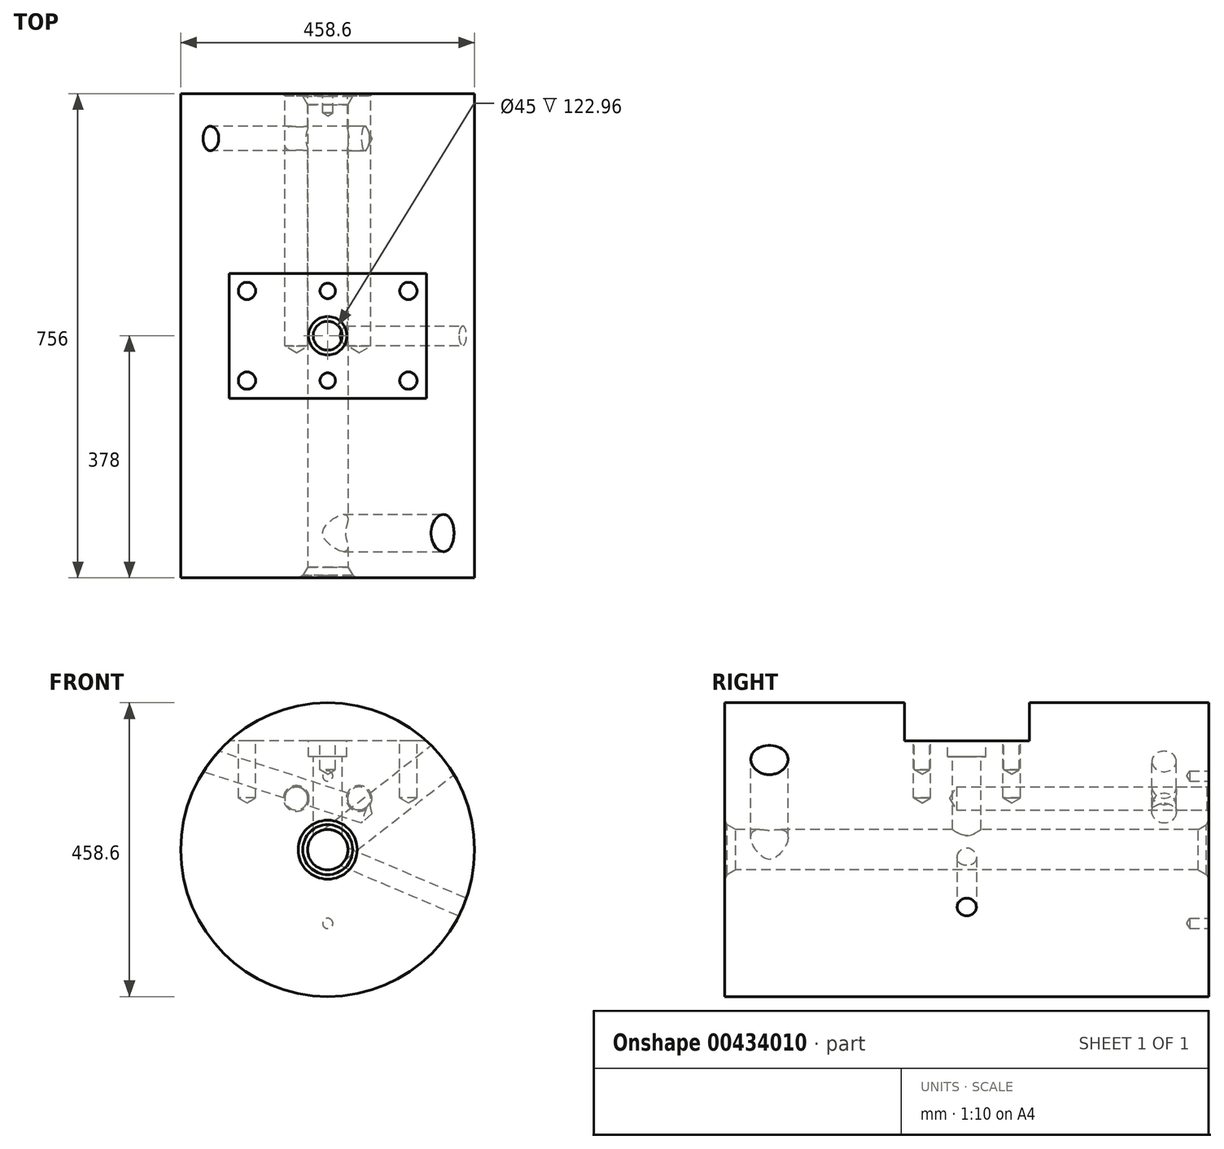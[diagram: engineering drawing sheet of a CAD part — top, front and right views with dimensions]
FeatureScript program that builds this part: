
annotation { "Feature Type Name" : "Feature", "Feature Type Description" : "" }
export const myFeature = defineFeature(function(context is Context, id is Id, definition is map)
    precondition{}
    {
        {
            var Q0;
            Q0=qCreatedBy(makeId("Front.planeOp"),FACE);
            var sketch = newSketch(context, id + "F0", { "sketchPlane" : qUnion([Q0])});
            skCircle(sketch, "E0", {"center": v(0, 0) * mm, "radius": 229.3 * mm});
            skSolve(sketch);
        }
        {
            var Q0;
            Q0=qCreatedBy(makeId("Right.planeOp"),FACE);
            var sketch = newSketch(context, id + "F1", { "sketchPlane" : qUnion([Q0])});
            skLineSegment(sketch, "E1", {"start": v(0, 0) * mm, "end": v(756, 0) * mm});
            skLineSegment(sketch, "E2", {"start": v(0, 0) * mm, "end": v(0, 229.3) * mm});
            skLineSegment(sketch, "E3", {"start": v(0, 229.3) * mm, "end": v(756, 229.3) * mm});
            skLineSegment(sketch, "E4", {"start": v(756, 0) * mm, "end": v(756, 229.3) * mm});
            skLineSegment(sketch, "E5.0", {"start": v(0, 31.5) * mm, "end": v(756, 31.5) * mm});
            skLineSegment(sketch, "E6", {"start": v(0, 46) * mm, "end": v(4, 39) * mm});
            skLineSegment(sketch, "E7", {"start": v(4, 39) * mm, "end": v(17, 31.5) * mm});
            skLineSegment(sketch, "E8", {"start": v(378, 229.3) * mm, "end": v(378, 142.86) * mm});
            skLineSegment(sketch, "E9.MirrorCS", {"start": v(756, 46) * mm, "end": v(752, 39) * mm});
            skLineSegment(sketch, "E10.MirrorCS", {"start": v(752, 39) * mm, "end": v(739, 31.5) * mm});
            skSolve(sketch);
        }
        {
            var Q0;
            {var subQ8=sQuery(id+"F1.wireOp",EDGE,"E6");Q0=makeQuery(id+"F1.imprint","IMPRINT",FACE,{"disambiguationData":[TD([[makeQuery(id+"F1.imprint","IMPRINT",EDGE,{"derivedFrom":subQ8}),1.0]])]});}
            var Q1;
            Q1=sQuery(id+"F1.wireOp",EDGE,"E1");
            revolve(context, id + "F2", {"entities" : qUnion([Q0]), "axis" : qUnion([Q1]), "revolveType" : RevolveType.FULL});
        }
        {
            var Q0;
            Q0=qCreatedBy(makeId("Right.planeOp"),FACE);
            var sketch = newSketch(context, id + "F3", { "sketchPlane" : qUnion([Q0])});
            skLineSegment(sketch, "E11", {"start": v(0, -229.3) * mm, "end": v(756, -229.3) * mm});
            skLineSegment(sketch, "E12", {"start": v(756, 229.3) * mm, "end": v(0, 229.3) * mm});
            skLineSegment(sketch, "E13", {"start": v(0, 0) * mm, "end": v(676.75, 0) * mm});
            skLineSegment(sketch, "E14.0", {"start": v(0, 170) * mm, "end": v(676.75, 170) * mm});
            skLineSegment(sketch, "E15", {"start": v(378, 229.3) * mm, "end": v(378, 170) * mm});
            skLineSegment(sketch, "E16.0", {"start": v(280.5, 229.3) * mm, "end": v(280.5, 170) * mm});
            skLineSegment(sketch, "E17.0", {"start": v(475.5, 229.3) * mm, "end": v(475.5, 170) * mm});
            skSolve(sketch);
        }
        {
            var Q0;
            {var subQ0=sQuery(id+"F3.wireOp",EDGE,"E15");Q0=makeQuery(id+"F3.imprint","IMPRINT",FACE,{"disambiguationData":[TD([[makeQuery(id+"F3.imprint","IMPRINT",EDGE,{"derivedFrom":subQ0}),-1.0]])]});}
            var Q1;
            {var subQ0=sQuery(id+"F3.wireOp",EDGE,"E15");Q1=makeQuery(id+"F3.imprint","IMPRINT",FACE,{"disambiguationData":[TD([[makeQuery(id+"F3.imprint","IMPRINT",EDGE,{"derivedFrom":subQ0}),1.0]])]});}
            extrude(context, id + "F4", {"entities" : qUnion([Q0, Q1]), "operationType" : NewBodyOperationType.REMOVE, "endBound" : BoundingType.SYMMETRIC, "depth" : 400 * mm});
        }
        {
            var Q0;
            Q0=makeQuery(id+"F4.boolean.opBoolean","COPY",FACE,{"derivedFrom":makeQuery(id+"F4.opExtrude","SWEPT_FACE",FACE,{"disambiguationData":[OSD([sQuery(id+"F3.wireOp",EDGE,"E14.0")])]})});
            var sketch = newSketch(context, id + "F5", { "sketchPlane" : qUnion([Q0])});
            skLineSegment(sketch, "E18", {"start": v(153.88, 0) * mm, "end": v(153.88, 280.5) * mm});
            skLineSegment(sketch, "E19", {"start": v(153.88, 280.5) * mm, "end": v(153.88, 475.5) * mm});
            skLineSegment(sketch, "E20", {"start": v(153.88, 475.5) * mm, "end": v(153.88, 756) * mm});
            skLineSegment(sketch, "E21", {"start": v(-153.88, 280.5) * mm, "end": v(-153.88, 0) * mm});
            skLineSegment(sketch, "E22", {"start": v(-153.88, 475.5) * mm, "end": v(-153.88, 280.5) * mm});
            skLineSegment(sketch, "E23", {"start": v(-153.88, 756) * mm, "end": v(-153.88, 475.5) * mm});
            skLineSegment(sketch, "E24", {"start": v(153.88, 280.5) * mm, "end": v(-153.88, 280.5) * mm});
            skLineSegment(sketch, "E25", {"start": v(153.88, 475.5) * mm, "end": v(153.88, 280.5) * mm});
            skLineSegment(sketch, "E26", {"start": v(153.88, 475.5) * mm, "end": v(-153.88, 475.5) * mm});
            skLineSegment(sketch, "E27", {"start": v(-153.88, 280.5) * mm, "end": v(-153.88, 475.5) * mm});
            skPoint(sketch, "E28", {"position": v(-126, 308) * mm});
            skPoint(sketch, "E29", {"position": v(0, 308) * mm});
            skPoint(sketch, "E30", {"position": v(126, 308) * mm});
            skPoint(sketch, "E31", {"position": v(-66, 378) * mm});
            skPoint(sketch, "E32", {"position": v(0, 378) * mm});
            skPoint(sketch, "E33", {"position": v(66, 378) * mm});
            skPoint(sketch, "E34", {"position": v(-153.88, 378) * mm});
            skLineSegment(sketch, "E35", {"start": v(-153.88, 378) * mm, "end": v(153.88, 378) * mm, "construction": true});
            skPoint(sketch, "E36", {"position": v(0, 280.5) * mm});
            skLineSegment(sketch, "E37", {"start": v(0, 280.5) * mm, "end": v(0, 378) * mm, "construction": true});
            skPoint(sketch, "E38.MirrorP", {"position": v(-126, 448) * mm});
            skPoint(sketch, "E39.MirrorP", {"position": v(0, 448) * mm});
            skPoint(sketch, "E40.MirrorP", {"position": v(126, 448) * mm});
            skSolve(sketch);
        }
        {
            var Q0;
            Q0=sQuery(id+"F5.wireOp",VERTEX,"E32");
            var Q1;
            Q1=makeQuery(id+"F2.opRevolve","SWEPT_BODY",BODY,{"disambiguationData":[OSD([sQuery(id+"F1.wireOp",EDGE,"E2"),sQuery(id+"F1.wireOp",EDGE,"E3"),sQuery(id+"F1.wireOp",EDGE,"E4"),sQuery(id+"F1.wireOp",EDGE,"E5.0"),sQuery(id+"F1.wireOp",EDGE,"E6"),sQuery(id+"F1.wireOp",EDGE,"E7"),sQuery(id+"F1.wireOp",EDGE,"E9.MirrorCS"),sQuery(id+"F1.wireOp",EDGE,"E10.MirrorCS")])]});
            hole(context, id + "F6", {"style" : HoleStyle.C_BORE, "endStyle" : HoleEndStyle.BLIND, "holeDiameter" : 45 * mm, "cBoreDiameter" : 60 * mm, "cBoreDepth" : 25 * mm, "holeDepth" : 170 * mm, "tappedDepth" : 12 * mm, "tapClearance" : 3, "startFromSketch" : true, "locations" : qUnion([Q0]), "scope" : qUnion([Q1])});
        }
        {
            var Q0;
            Q0=sQuery(id+"F5.wireOp",VERTEX,"E29");
            var Q1;
            Q1=sQuery(id+"F5.wireOp",VERTEX,"E39.MirrorP");
            var Q2;
            Q2=makeQuery(id+"F2.opRevolve","SWEPT_BODY",BODY,{"disambiguationData":[OSD([sQuery(id+"F1.wireOp",EDGE,"E2"),sQuery(id+"F1.wireOp",EDGE,"E3"),sQuery(id+"F1.wireOp",EDGE,"E4"),sQuery(id+"F1.wireOp",EDGE,"E5.0"),sQuery(id+"F1.wireOp",EDGE,"E6"),sQuery(id+"F1.wireOp",EDGE,"E7"),sQuery(id+"F1.wireOp",EDGE,"E9.MirrorCS"),sQuery(id+"F1.wireOp",EDGE,"E10.MirrorCS")])]});
            hole(context, id + "F7", {"style" : HoleStyle.SIMPLE, "endStyle" : HoleEndStyle.BLIND, "holeDiameter" : 24 * mm, "holeDepth" : 45 * mm, "tappedDepth" : 12 * mm, "tapClearance" : 3, "startFromSketch" : true, "locations" : qUnion([Q0, Q1]), "scope" : qUnion([Q2])});
        }
        {
            var Q0;
            Q0=sQuery(id+"F5.wireOp",VERTEX,"E28");
            var Q1;
            Q1=sQuery(id+"F5.wireOp",VERTEX,"E38.MirrorP");
            var Q2;
            Q2=sQuery(id+"F5.wireOp",VERTEX,"E40.MirrorP");
            var Q3;
            Q3=sQuery(id+"F5.wireOp",VERTEX,"E30");
            var Q4;
            Q4=makeQuery(id+"F2.opRevolve","SWEPT_BODY",BODY,{"disambiguationData":[OSD([sQuery(id+"F1.wireOp",EDGE,"E2"),sQuery(id+"F1.wireOp",EDGE,"E3"),sQuery(id+"F1.wireOp",EDGE,"E4"),sQuery(id+"F1.wireOp",EDGE,"E5.0"),sQuery(id+"F1.wireOp",EDGE,"E6"),sQuery(id+"F1.wireOp",EDGE,"E7"),sQuery(id+"F1.wireOp",EDGE,"E9.MirrorCS"),sQuery(id+"F1.wireOp",EDGE,"E10.MirrorCS")])]});
            hole(context, id + "F8", {"style" : HoleStyle.SIMPLE, "endStyle" : HoleEndStyle.BLIND, "holeDiameter" : 27 * mm, "holeDepth" : 89 * mm, "tappedDepth" : 12 * mm, "tapClearance" : 3, "startFromSketch" : true, "locations" : qUnion([Q0, Q1, Q2, Q3]), "scope" : qUnion([Q4])});
        }
        {
            var Q0;
            Q0=sQuery(id+"F5.wireOp",EDGE,"E35");
            cPlane(context, id + "F9", {"entities" : qUnion([Q0]), "cplaneType" : CPlaneType.LINE_ANGLE, "offset" : 25 * mm, "angle" : 0 * degree, "width" : 150 * mm, "height" : 150 * mm});
        }
        {
            var Q0;
            Q0=qCreatedBy(id+"F9.planeOp",FACE);
            var sketch = newSketch(context, id + "F10", { "sketchPlane" : qUnion([Q0])});
            skArc(sketch, "E41", {"start": v(-153.88, 170) * mm, "mid": v(0, -229.3) * mm, "end": v(153.88, 170) * mm});
            skLineSegment(sketch, "E42", {"start": v(153.88, 170) * mm, "end": v(-153.88, 170) * mm});
            skLineSegment(sketch, "E43", {"start": v(0, 0) * mm, "end": v(-211.07, -89.6) * mm});
            skPoint(sketch, "E44", {"position": v(-211.07, -89.6) * mm});
            skSolve(sketch);
        }
        {
            var Q0;
            Q0=sQuery(id+"F10.wireOp",VERTEX,"E44");
            var Q1;
            Q1=sQuery(id+"F10.wireOp",EDGE,"E43");
            cPlane(context, id + "F11", {"entities" : qUnion([Q0, Q1]), "cplaneType" : CPlaneType.LINE_POINT, "offset" : 25 * mm, "width" : 150 * mm, "height" : 150 * mm});
        }
        {
            var Q0;
            Q0=qCreatedBy(id+"F11.planeOp",FACE);
            var sketch = newSketch(context, id + "F12", { "sketchPlane" : qUnion([Q0])});
            skPoint(sketch, "E45.0", {"position": v(378, 0) * mm});
            skSolve(sketch);
        }
        {
            var Q0;
            Q0=sQuery(id+"F12.wireOp",VERTEX,"E45.0");
            var Q1;
            Q1=makeQuery(id+"F2.opRevolve","SWEPT_BODY",BODY,{"disambiguationData":[OSD([sQuery(id+"F1.wireOp",EDGE,"E2"),sQuery(id+"F1.wireOp",EDGE,"E3"),sQuery(id+"F1.wireOp",EDGE,"E4"),sQuery(id+"F1.wireOp",EDGE,"E5.0"),sQuery(id+"F1.wireOp",EDGE,"E6"),sQuery(id+"F1.wireOp",EDGE,"E7"),sQuery(id+"F1.wireOp",EDGE,"E9.MirrorCS"),sQuery(id+"F1.wireOp",EDGE,"E10.MirrorCS")])]});
            hole(context, id + "F13", {"style" : HoleStyle.SIMPLE, "endStyle" : HoleEndStyle.BLIND, "holeDiameter" : 30 * mm, "holeDepth" : 229 * mm, "tappedDepth" : 12 * mm, "tapClearance" : 3, "startFromSketch" : true, "locations" : qUnion([Q0]), "scope" : qUnion([Q1])});
        }
        {
            var Q0;
            Q0=makeQuery(id+"F2.opRevolve","SWEPT_FACE",FACE,{"disambiguationData":[OSD([sQuery(id+"F1.wireOp",EDGE,"E2")])]});
            cPlane(context, id + "F14", {"entities" : qUnion([Q0]), "cplaneType" : CPlaneType.OFFSET, "offset" : 70 * mm, "oppositeDirection" : true, "width" : 150 * mm, "height" : 150 * mm});
        }
        {
            var Q0;
            Q0=qCreatedBy(id+"F14.planeOp",FACE);
            var sketch = newSketch(context, id + "F15", { "sketchPlane" : qUnion([Q0])});
            skCircle(sketch, "E46", {"center": v(0, 0) * mm, "radius": 229.3 * mm});
            skLineSegment(sketch, "E47.0", {"start": v(-153.88, 170) * mm, "end": v(153.88, 170) * mm});
            skLineSegment(sketch, "E48", {"start": v(0, 0) * mm, "end": v(180.7, 141.17) * mm});
            skSolve(sketch);
        }
        {
            var Q0;
            Q0=sQuery(id+"F15.wireOp",VERTEX,"E48.end");
            var Q1;
            Q1=sQuery(id+"F15.wireOp",EDGE,"E48");
            cPlane(context, id + "F16", {"entities" : qUnion([Q0, Q1]), "cplaneType" : CPlaneType.LINE_POINT, "offset" : 25 * mm, "width" : 150 * mm, "height" : 150 * mm});
        }
        {
            var Q0;
            Q0=qCreatedBy(id+"F16.planeOp",FACE);
            var sketch = newSketch(context, id + "F17", { "sketchPlane" : qUnion([Q0])});
            skPoint(sketch, "E49.0", {"position": v(70, 0) * mm});
            skSolve(sketch);
        }
        {
            var Q0;
            Q0=sQuery(id+"F17.wireOp",VERTEX,"E49.0");
            var Q1;
            Q1=makeQuery(id+"F2.opRevolve","SWEPT_BODY",BODY,{"disambiguationData":[OSD([sQuery(id+"F1.wireOp",EDGE,"E2"),sQuery(id+"F1.wireOp",EDGE,"E3"),sQuery(id+"F1.wireOp",EDGE,"E4"),sQuery(id+"F1.wireOp",EDGE,"E5.0"),sQuery(id+"F1.wireOp",EDGE,"E6"),sQuery(id+"F1.wireOp",EDGE,"E7"),sQuery(id+"F1.wireOp",EDGE,"E9.MirrorCS"),sQuery(id+"F1.wireOp",EDGE,"E10.MirrorCS")])]});
            hole(context, id + "F18", {"style" : HoleStyle.SIMPLE, "endStyle" : HoleEndStyle.BLIND, "holeDiameter" : 58 * mm, "holeDepth" : 229 * mm, "tappedDepth" : 12 * mm, "tapClearance" : 3, "startFromSketch" : true, "locations" : qUnion([Q0]), "scope" : qUnion([Q1])});
        }
        {
            var Q0;
            Q0=makeQuery(id+"F2.opRevolve","SWEPT_FACE",FACE,{"disambiguationData":[OSD([sQuery(id+"F1.wireOp",EDGE,"E4")])]});
            cPlane(context, id + "F19", {"entities" : qUnion([Q0]), "cplaneType" : CPlaneType.OFFSET, "offset" : 70 * mm, "oppositeDirection" : true, "width" : 150 * mm, "height" : 150 * mm});
        }
        {
            var Q0;
            Q0=qCreatedBy(id+"F19.planeOp",FACE);
            var sketch = newSketch(context, id + "F20", { "sketchPlane" : qUnion([Q0])});
            skCircle(sketch, "E50", {"center": v(0, 0) * mm, "radius": 229.3 * mm});
            skPoint(sketch, "E51", {"position": v(183.12, 138) * mm});
            skLineSegment(sketch, "E52", {"start": v(183.12, 138) * mm, "end": v(46.4, 93.58) * mm});
            skSolve(sketch);
        }
        {
            var Q0;
            Q0=sQuery(id+"F20.wireOp",VERTEX,"E51");
            var Q1;
            Q1=sQuery(id+"F20.wireOp",EDGE,"E52");
            cPlane(context, id + "F21", {"entities" : qUnion([Q0, Q1]), "cplaneType" : CPlaneType.LINE_POINT, "offset" : 25 * mm, "width" : 150 * mm, "height" : 150 * mm});
        }
        {
            var Q0;
            Q0=qCreatedBy(id+"F21.planeOp",FACE);
            var sketch = newSketch(context, id + "F22", { "sketchPlane" : qUnion([Q0])});
            skPoint(sketch, "E53.0", {"position": v(686, 74.66) * mm});
            skSolve(sketch);
        }
        {
            var Q0;
            Q0=sQuery(id+"F22.wireOp",VERTEX,"E53.0");
            var Q1;
            Q1=makeQuery(id+"F2.opRevolve","SWEPT_BODY",BODY,{"disambiguationData":[OSD([sQuery(id+"F1.wireOp",EDGE,"E2"),sQuery(id+"F1.wireOp",EDGE,"E3"),sQuery(id+"F1.wireOp",EDGE,"E4"),sQuery(id+"F1.wireOp",EDGE,"E5.0"),sQuery(id+"F1.wireOp",EDGE,"E6"),sQuery(id+"F1.wireOp",EDGE,"E7"),sQuery(id+"F1.wireOp",EDGE,"E9.MirrorCS"),sQuery(id+"F1.wireOp",EDGE,"E10.MirrorCS")])]});
            hole(context, id + "F23", {"style" : HoleStyle.SIMPLE, "endStyle" : HoleEndStyle.BLIND, "oppositeDirection" : true, "holeDiameter" : 38 * mm, "holeDepth" : 254 * mm, "tappedDepth" : 12 * mm, "tapClearance" : 3, "startFromSketch" : true, "locations" : qUnion([Q0]), "scope" : qUnion([Q1])});
        }
        {
            var Q0;
            Q0=sQuery(id+"F22.wireOp",VERTEX,"E53.0");
            var Q1;
            Q1=makeQuery(id+"F2.opRevolve","SWEPT_BODY",BODY,{"disambiguationData":[OSD([sQuery(id+"F1.wireOp",EDGE,"E2"),sQuery(id+"F1.wireOp",EDGE,"E3"),sQuery(id+"F1.wireOp",EDGE,"E4"),sQuery(id+"F1.wireOp",EDGE,"E5.0"),sQuery(id+"F1.wireOp",EDGE,"E6"),sQuery(id+"F1.wireOp",EDGE,"E7"),sQuery(id+"F1.wireOp",EDGE,"E9.MirrorCS"),sQuery(id+"F1.wireOp",EDGE,"E10.MirrorCS")])]});
            hole(context, id + "F24", {"style" : HoleStyle.SIMPLE, "endStyle" : HoleEndStyle.BLIND, "holeDiameter" : 38 * mm, "holeDepth" : 50 * mm, "tappedDepth" : 12 * mm, "tapClearance" : 3, "startFromSketch" : true, "locations" : qUnion([Q0]), "scope" : qUnion([Q1])});
        }
        {
            var Q0;
            Q0=makeQuery(id+"F2.opRevolve","SWEPT_FACE",FACE,{"disambiguationData":[OSD([sQuery(id+"F1.wireOp",EDGE,"E4")])]});
            var sketch = newSketch(context, id + "F25", { "sketchPlane" : qUnion([Q0])});
            skPoint(sketch, "E54", {"position": v(-49, 80) * mm});
            skPoint(sketch, "E55", {"position": v(49, 80) * mm});
            skPoint(sketch, "E56", {"position": v(0, 115) * mm});
            skPoint(sketch, "E57", {"position": v(0, -115) * mm});
            skPoint(sketch, "E58", {"position": v(70, -182) * mm});
            skSolve(sketch);
        }
        {
            var Q0;
            Q0=sQuery(id+"F25.wireOp",VERTEX,"E56");
            var Q1;
            Q1=sQuery(id+"F25.wireOp",VERTEX,"E57");
            var Q2;
            Q2=makeQuery(id+"F2.opRevolve","SWEPT_BODY",BODY,{"disambiguationData":[OSD([sQuery(id+"F1.wireOp",EDGE,"E2"),sQuery(id+"F1.wireOp",EDGE,"E3"),sQuery(id+"F1.wireOp",EDGE,"E4"),sQuery(id+"F1.wireOp",EDGE,"E5.0"),sQuery(id+"F1.wireOp",EDGE,"E6"),sQuery(id+"F1.wireOp",EDGE,"E7"),sQuery(id+"F1.wireOp",EDGE,"E9.MirrorCS"),sQuery(id+"F1.wireOp",EDGE,"E10.MirrorCS")])]});
            hole(context, id + "F26", {"style" : HoleStyle.SIMPLE, "endStyle" : HoleEndStyle.BLIND, "holeDiameter" : 16 * mm, "holeDepth" : 30 * mm, "tappedDepth" : 12 * mm, "tapClearance" : 3, "startFromSketch" : true, "locations" : qUnion([Q0, Q1]), "scope" : qUnion([Q2])});
        }
        {
            var Q0;
            Q0=sQuery(id+"F25.wireOp",VERTEX,"E54");
            var Q1;
            Q1=sQuery(id+"F25.wireOp",VERTEX,"E55");
            var Q2;
            Q2=makeQuery(id+"F2.opRevolve","SWEPT_BODY",BODY,{"disambiguationData":[OSD([sQuery(id+"F1.wireOp",EDGE,"E2"),sQuery(id+"F1.wireOp",EDGE,"E3"),sQuery(id+"F1.wireOp",EDGE,"E4"),sQuery(id+"F1.wireOp",EDGE,"E5.0"),sQuery(id+"F1.wireOp",EDGE,"E6"),sQuery(id+"F1.wireOp",EDGE,"E7"),sQuery(id+"F1.wireOp",EDGE,"E9.MirrorCS"),sQuery(id+"F1.wireOp",EDGE,"E10.MirrorCS")])]});
            hole(context, id + "F27", {"style" : HoleStyle.C_SINK, "endStyle" : HoleEndStyle.BLIND, "holeDiameter" : 36 * mm, "cSinkDiameter" : 40 * mm, "cSinkAngle" : 60 * degree, "holeDepth" : 394 * mm, "tappedDepth" : 12 * mm, "tapClearance" : 3, "startFromSketch" : true, "locations" : qUnion([Q0, Q1]), "scope" : qUnion([Q2])});
        }
    });
